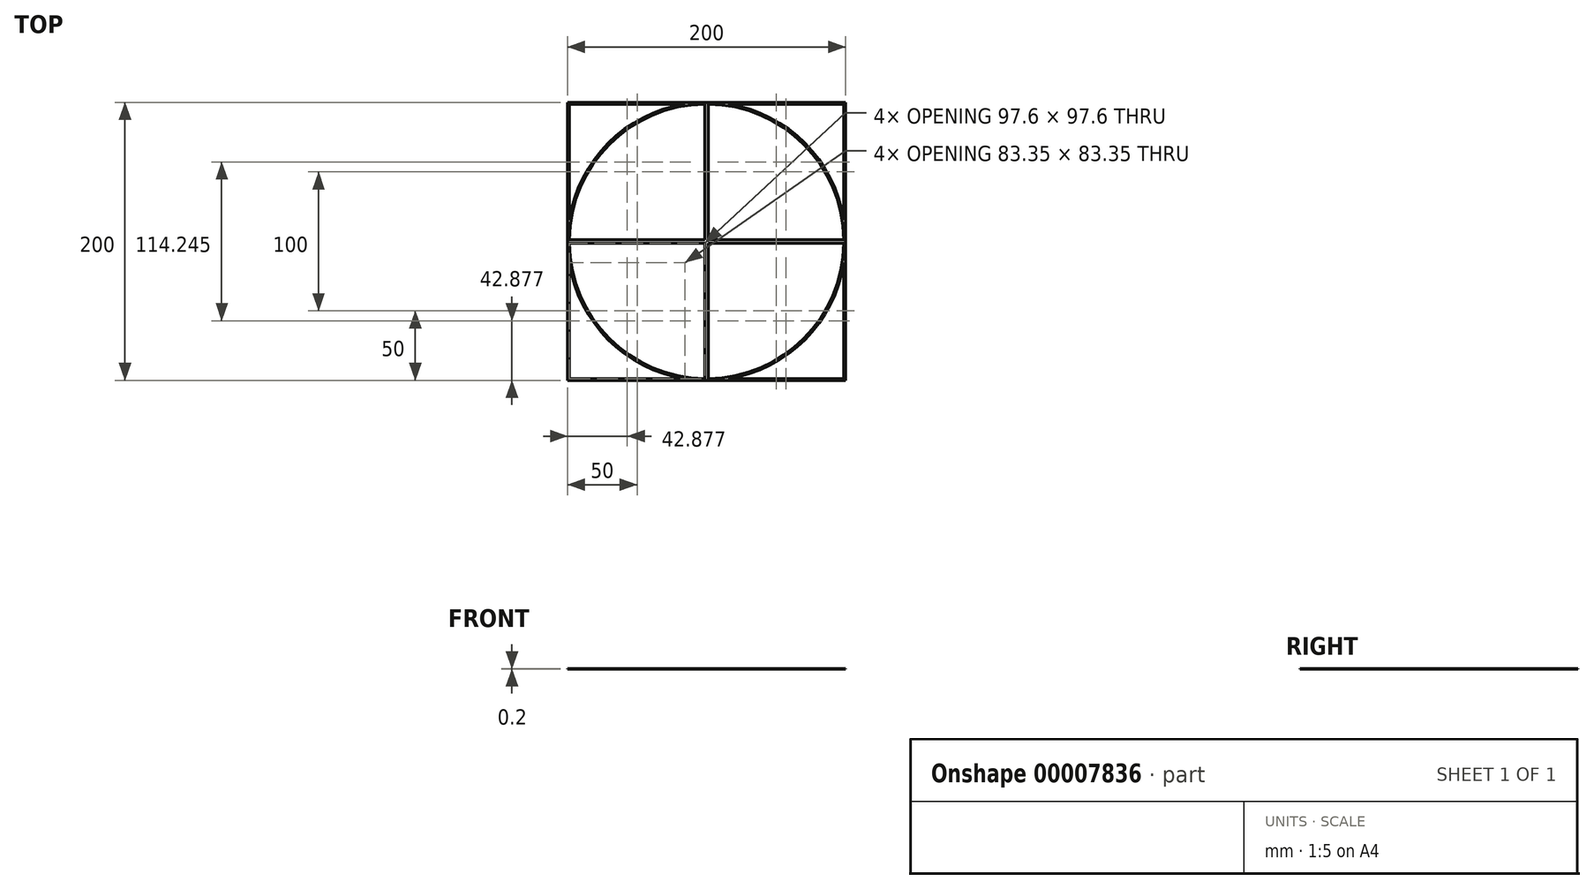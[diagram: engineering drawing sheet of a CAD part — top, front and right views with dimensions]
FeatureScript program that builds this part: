
annotation { "Feature Type Name" : "Feature", "Feature Type Description" : "" }
export const myFeature = defineFeature(function(context is Context, id is Id, definition is map)
    precondition{}
    {
        {
            var Q0;
            Q0=qCreatedBy(makeId("Top.planeOp"),FACE);
            var sketch = newSketch(context, id + "F0", { "sketchPlane" : qUnion([Q0])});
            skLineSegment(sketch, "E0.top", {"start": v(0, 100) * mm, "end": v(100, 100) * mm});
            skLineSegment(sketch, "E0.right", {"start": v(100, 0) * mm, "end": v(100, 100) * mm});
            skLineSegment(sketch, "E1.top", {"start": v(0, 100) * mm, "end": v(-100, 100) * mm});
            skLineSegment(sketch, "E1.left", {"start": v(0, 98.8) * mm, "end": v(0, 100) * mm});
            skLineSegment(sketch, "E1.right", {"start": v(-100, 0) * mm, "end": v(-100, 100) * mm});
            skLineSegment(sketch, "E2.top", {"start": v(0, -100) * mm, "end": v(-100, -100) * mm});
            skLineSegment(sketch, "E2.right", {"start": v(-100, 0) * mm, "end": v(-100, -100) * mm});
            skLineSegment(sketch, "E3.top", {"start": v(0, -100) * mm, "end": v(100, -100) * mm});
            skLineSegment(sketch, "E3.right", {"start": v(100, 0) * mm, "end": v(100, -100) * mm});
            skLineSegment(sketch, "E4.0", {"start": v(-98.8, 15.45) * mm, "end": v(-98.8, 98.8) * mm});
            skLineSegment(sketch, "E4.1", {"start": v(-1.2, 1.2) * mm, "end": v(-98.8, 1.2) * mm});
            skLineSegment(sketch, "E4.2", {"start": v(-1.2, 1.2) * mm, "end": v(-1.2, 98.8) * mm});
            skLineSegment(sketch, "E4.3", {"start": v(-15.45, 98.8) * mm, "end": v(-98.8, 98.8) * mm});
            skLineSegment(sketch, "E5.0", {"start": v(15.45, 98.8) * mm, "end": v(98.8, 98.8) * mm});
            skLineSegment(sketch, "E5.1", {"start": v(1.2, 1.2) * mm, "end": v(1.2, 98.8) * mm});
            skLineSegment(sketch, "E5.2", {"start": v(1.2, 1.2) * mm, "end": v(98.8, 1.2) * mm});
            skLineSegment(sketch, "E5.3", {"start": v(98.8, 15.45) * mm, "end": v(98.8, 98.8) * mm});
            skLineSegment(sketch, "E6.0", {"start": v(1.2, -1.2) * mm, "end": v(1.2, -98.8) * mm});
            skLineSegment(sketch, "E6.1", {"start": v(1.2, -1.2) * mm, "end": v(98.8, -1.2) * mm});
            skLineSegment(sketch, "E6.2", {"start": v(98.8, -15.45) * mm, "end": v(98.8, -98.8) * mm});
            skLineSegment(sketch, "E6.3", {"start": v(15.45, -98.8) * mm, "end": v(98.8, -98.8) * mm});
            skLineSegment(sketch, "E7.0", {"start": v(-98.8, -15.45) * mm, "end": v(-98.8, -98.8) * mm});
            skLineSegment(sketch, "E7.1", {"start": v(-1.2, -1.2) * mm, "end": v(-98.8, -1.2) * mm});
            skLineSegment(sketch, "E7.2", {"start": v(-1.2, -1.2) * mm, "end": v(-1.2, -98.8) * mm});
            skLineSegment(sketch, "E7.3", {"start": v(-15.45, -98.8) * mm, "end": v(-98.8, -98.8) * mm});
            skArc(sketch, "E8", {"start": v(-98.8, -1.2) * mm, "mid": v(-69.87, -69.87) * mm, "end": v(-1.2, -98.8) * mm});
            skArc(sketch, "E9", {"start": v(98.8, 15.45) * mm, "mid": v(70.71, 70.71) * mm, "end": v(15.45, 98.8) * mm});
            skArc(sketch, "E10.trimOffspring", {"start": v(-15.45, 98.8) * mm, "mid": v(-70.71, 70.71) * mm, "end": v(-98.8, 15.45) * mm});
            skArc(sketch, "E11.trimOffspring", {"start": v(1.2, -98.8) * mm, "mid": v(69.87, 69.87) * mm, "end": v(-98.8, 1.2) * mm});
            skArc(sketch, "E12.trimOffspring", {"start": v(15.45, -98.8) * mm, "mid": v(70.71, -70.71) * mm, "end": v(98.8, -15.45) * mm});
            skArc(sketch, "E13.trimOffspring", {"start": v(-98.8, -15.45) * mm, "mid": v(-70.71, -70.71) * mm, "end": v(-15.45, -98.8) * mm});
            skSolve(sketch);
        }
        {
            var Q0;
            Q0=makeQuery(id+"F0.imprint","IMPRINT",FACE,{"disambiguationData":[TD([[makeQuery(id+"F0.imprint","IMPRINT",EDGE,{"derivedFrom":sQuery(id+"F0.wireOp",EDGE,"E0.top")}),-1.0]])]});
            extrude(context, id + "F1", {"entities" : qUnion([Q0]), "depth" : 0.2 * mm});
        }
    });
